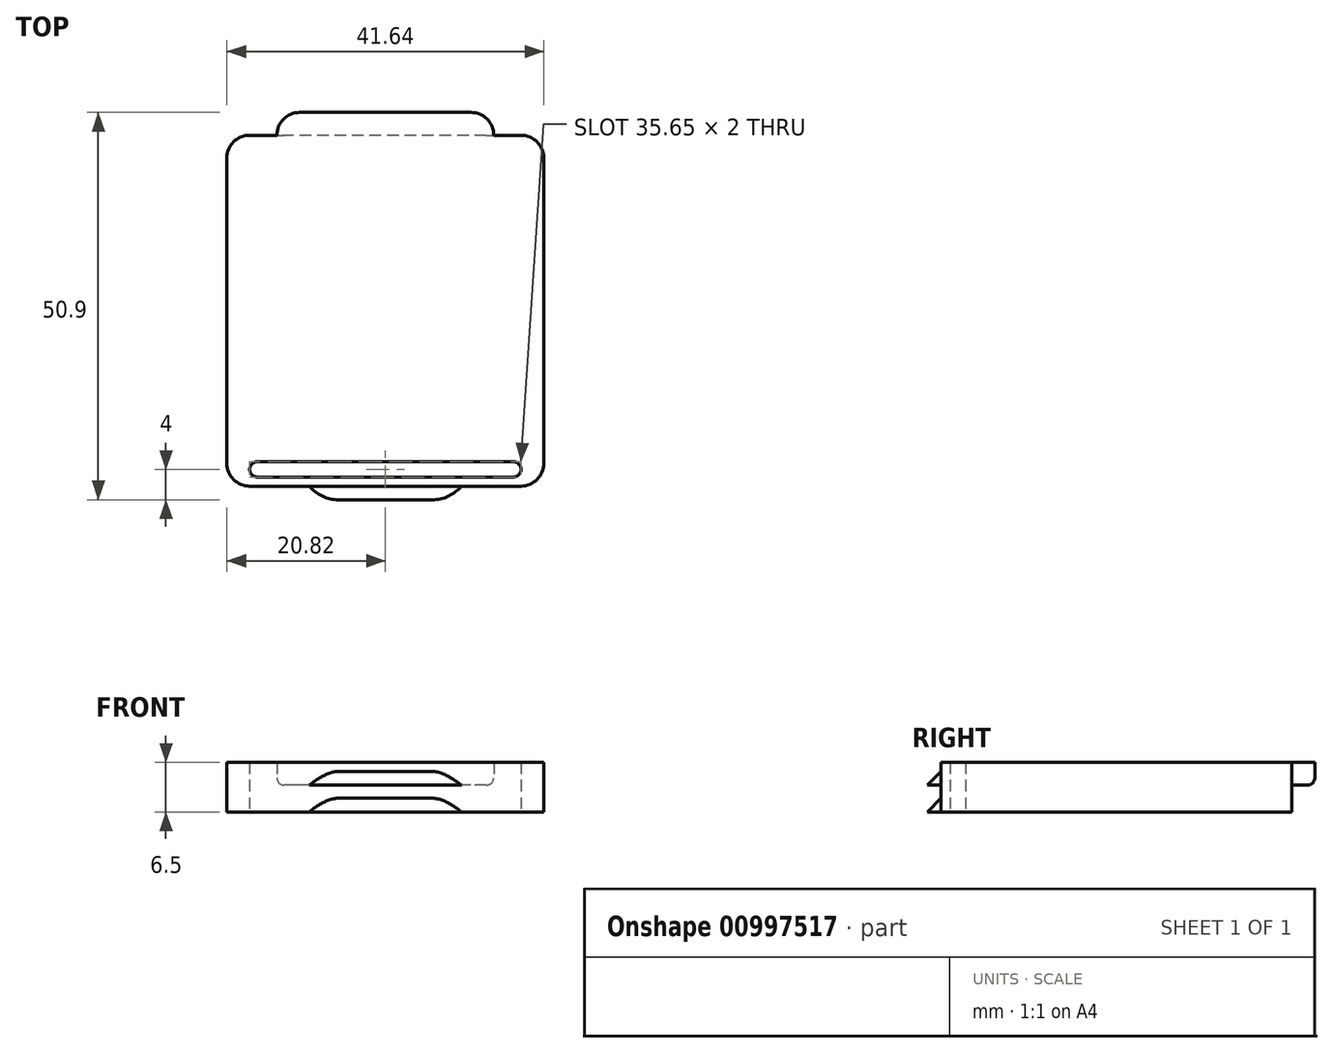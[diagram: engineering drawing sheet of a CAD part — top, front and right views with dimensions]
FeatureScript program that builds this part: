
annotation { "Feature Type Name" : "Feature", "Feature Type Description" : "" }
export const myFeature = defineFeature(function(context is Context, id is Id, definition is map)
    precondition{}
    {
        {
            var Q0;
            Q0=qCreatedBy(makeId("Top.planeOp"),FACE);
            var sketch = newSketch(context, id + "F0", { "sketchPlane" : qUnion([Q0])});
            skLineSegment(sketch, "E0.bottom", {"start": v(20.82, 23.05) * mm, "end": v(-20.83, 23.05) * mm});
            skLineSegment(sketch, "E0.top", {"start": v(20.83, -23.05) * mm, "end": v(-20.82, -23.05) * mm});
            skLineSegment(sketch, "E0.left", {"start": v(20.82, 23.05) * mm, "end": v(20.83, -23.05) * mm});
            skLineSegment(sketch, "E0.right", {"start": v(-20.83, 23.05) * mm, "end": v(-20.82, -23.05) * mm});
            skPoint(sketch, "E0.middle", {"position": v(0, 0) * mm});
            skPoint(sketch, "E1.visualSharp", {"position": v(-20.83, 23.05) * mm});
            skPoint(sketch, "E2.visualSharp", {"position": v(20.82, 23.05) * mm});
            skPoint(sketch, "E3.visualSharp", {"position": v(20.83, -23.05) * mm});
            skPoint(sketch, "E4.visualSharp", {"position": v(-20.82, -23.05) * mm});
            skLineSegment(sketch, "E5.0", {"start": v(16.83, -21.85) * mm, "end": v(-16.82, -21.85) * mm});
            skLineSegment(sketch, "E6.0", {"start": v(16.83, -19.85) * mm, "end": v(-16.82, -19.85) * mm});
            skArc(sketch, "E7", {"start": v(16.83, -21.85) * mm, "mid": v(17.83, -20.85) * mm, "end": v(16.83, -19.85) * mm});
            skArc(sketch, "E8", {"start": v(-16.82, -19.85) * mm, "mid": v(-17.82, -20.85) * mm, "end": v(-16.82, -21.85) * mm});
            skSolve(sketch);
        }
        {
            var Q0;
            Q0 = qSketchRegion(id + "F0", true);
            extrude(context, id + "F1", {"entities" : qUnion([Q0]), "depth" : 6.5 * mm, "offsetDistance" : 25 * mm});
        }
        {
            var Q0;
            Q0=makeQuery(id+"F1.opExtrude","SWEPT_FACE",FACE,{"disambiguationData":[OSD([sQuery(id+"F0.wireOp",EDGE,"E0.bottom")])]});
            var sketch = newSketch(context, id + "F2", { "sketchPlane" : qUnion([Q0])});
            skLineSegment(sketch, "E9.bottom", {"start": v(-14.25, 6.5) * mm, "end": v(14.25, 6.5) * mm});
            skLineSegment(sketch, "E9.top", {"start": v(-14.25, 3.5) * mm, "end": v(14.25, 3.5) * mm});
            skLineSegment(sketch, "E9.left", {"start": v(-14.25, 6.5) * mm, "end": v(-14.25, 3.5) * mm});
            skLineSegment(sketch, "E9.right", {"start": v(14.25, 6.5) * mm, "end": v(14.25, 3.5) * mm});
            skPoint(sketch, "E9.middle.positionSnap0", {"position": v(0, 6.5) * mm});
            skSolve(sketch);
        }
        {
            var Q0;
            Q0 = qSketchRegion(id + "F2", true);
            extrude(context, id + "F3", {"entities" : qUnion([Q0]), "operationType" : NewBodyOperationType.ADD, "depth" : 3 * mm, "offsetDistance" : 25 * mm});
        }
        {
            var Q0;
            Q0=makeQuery(id+"F3.opExtrude","SWEPT_EDGE",EDGE,{"disambiguationData":[OSD([sQuery(id+"F2.wireOp",EDGE,"E9.top"),sQuery(id+"F2.wireOp",EDGE,"E9.right")])]});
            var Q1;
            Q1=makeQuery(id+"F3.opExtrude","SWEPT_EDGE",EDGE,{"disambiguationData":[OSD([sQuery(id+"F2.wireOp",EDGE,"E9.top"),sQuery(id+"F2.wireOp",EDGE,"E9.left")])]});
            var Q2;
            Q2=makeQuery(id+"F3.opExtrude","CAP_EDGE",EDGE,{"disambiguationData":[OSD([sQuery(id+"F2.wireOp",EDGE,"E9.top")])],"isStart":false});
            fillet(context, id + "F4", {"entities" : qUnion([Q0, Q1, Q2]), "radius" : 1 * mm, "tangentPropagation" : true, "allowEdgeOverflow" : false});
        }
        {
            var Q0;
            Q0=makeQuery(id+"F3.opExtrude","CAP_EDGE",EDGE,{"disambiguationData":[OSD([sQuery(id+"F2.wireOp",EDGE,"E9.left")])],"isStart":false});
            var Q1;
            Q1=makeQuery(id+"F3.opExtrude","CAP_EDGE",EDGE,{"disambiguationData":[OSD([sQuery(id+"F2.wireOp",EDGE,"E9.right")])],"isStart":false});
            var Q2;
            {var subQ0=sQuery(id+"F2.wireOp",EDGE,"E9.top");Q2=makeQuery(id+"F4.opFillet","BLEND_EDGE",EDGE,{"blendedFrom":[makeQuery(id+"F3.opExtrude","SWEPT_EDGE",EDGE,{"disambiguationData":[OSD([subQ0,sQuery(id+"F2.wireOp",EDGE,"E9.right")])]}),makeQuery(id+"F3.opExtrude","CAP_EDGE",EDGE,{"disambiguationData":[OSD([subQ0])],"isStart":false})],"blendedInto":[]});}
            fillet(context, id + "F5", {"entities" : qUnion([Q0, Q1, Q2]), "radius" : 3 * mm, "tangentPropagation" : true, "defaultsChanged" : true, "vertexSettings" : [], "allowEdgeOverflow" : false});
        }
        {
            var Q0;
            Q0=makeQuery(id+"F1.opExtrude","SWEPT_FACE",FACE,{"disambiguationData":[OSD([sQuery(id+"F0.wireOp",EDGE,"E0.top")])]});
            var sketch = newSketch(context, id + "F6", { "sketchPlane" : qUnion([Q0])});
            skLineSegment(sketch, "E10.bottom", {"start": v(-10, 5.3) * mm, "end": v(10, 5.3) * mm});
            skLineSegment(sketch, "E10.top", {"start": v(-10, 3.5) * mm, "end": v(10, 3.5) * mm});
            skLineSegment(sketch, "E10.left", {"start": v(-10, 5.3) * mm, "end": v(-10, 3.5) * mm});
            skLineSegment(sketch, "E10.right", {"start": v(10, 5.3) * mm, "end": v(10, 3.5) * mm});
            skPoint(sketch, "E10.middle", {"position": v(0, 4.4) * mm});
            skPoint(sketch, "E10.middle.positionSnap0", {"position": v(0, 6.5) * mm});
            skPoint(sketch, "E10.centerSnap0", {"position": v(0, 6.5) * mm});
            skLineSegment(sketch, "E11.bottom", {"start": v(-10, 1.8) * mm, "end": v(10, 1.8) * mm});
            skLineSegment(sketch, "E11.top", {"start": v(-10, 0) * mm, "end": v(10, 0) * mm});
            skLineSegment(sketch, "E11.left", {"start": v(-10, 1.8) * mm, "end": v(-10, 0) * mm});
            skLineSegment(sketch, "E11.right", {"start": v(10, 1.8) * mm, "end": v(10, 0) * mm});
            skPoint(sketch, "E11.middle", {"position": v(0, 0.9) * mm});
            skSolve(sketch);
        }
        {
            var Q0;
            Q0 = qSketchRegion(id + "F6", true);
            extrude(context, id + "F7", {"entities" : qUnion([Q0]), "operationType" : NewBodyOperationType.ADD, "depth" : 1.8 * mm, "offsetDistance" : 25 * mm});
        }
        {
            var Q0;
            Q0=makeQuery(id+"F7.opExtrude","CAP_EDGE",EDGE,{"disambiguationData":[OSD([sQuery(id+"F6.wireOp",EDGE,"E10.left")])],"isStart":false});
            var Q1;
            Q1=makeQuery(id+"F7.opExtrude","CAP_EDGE",EDGE,{"disambiguationData":[OSD([sQuery(id+"F6.wireOp",EDGE,"E10.right")])],"isStart":false});
            var Q2;
            Q2=makeQuery(id+"F7.opExtrude","CAP_EDGE",EDGE,{"disambiguationData":[OSD([sQuery(id+"F6.wireOp",EDGE,"E11.left")])],"isStart":false});
            var Q3;
            Q3=makeQuery(id+"F7.opExtrude","CAP_EDGE",EDGE,{"disambiguationData":[OSD([sQuery(id+"F6.wireOp",EDGE,"E11.right")])],"isStart":false});
            fillet(context, id + "F8", {"entities" : qUnion([Q0, Q1, Q2, Q3]), "tangentPropagation" : true, "radius" : 5 * mm, "defaultsChanged" : true, "vertexSettings" : [], "allowEdgeOverflow" : false});
        }
        {
            var Q0;
            Q0=makeQuery(id+"F7.opExtrude","CAP_EDGE",EDGE,{"disambiguationData":[OSD([sQuery(id+"F6.wireOp",EDGE,"E10.bottom")])],"isStart":false});
            var Q1;
            Q1=makeQuery(id+"F7.opExtrude","CAP_EDGE",EDGE,{"disambiguationData":[OSD([sQuery(id+"F6.wireOp",EDGE,"E11.bottom")])],"isStart":false});
            chamfer(context, id + "F9", {"entities" : qUnion([Q0, Q1]), "chamferType" : ChamferType.TWO_OFFSETS, "width1" : 1.8 * mm, "oppositeDirection" : false, "width2" : 1.8 * mm, "tangentPropagation" : true});
        }
        {
            var Q0;
            Q0=makeQuery(id+"F1.opExtrude","SWEPT_EDGE",EDGE,{"disambiguationData":[OSD([sQuery(id+"F0.wireOp",EDGE,"E0.top"),sQuery(id+"F0.wireOp",EDGE,"E0.left")])]});
            var Q1;
            Q1=makeQuery(id+"F1.opExtrude","SWEPT_EDGE",EDGE,{"disambiguationData":[OSD([sQuery(id+"F0.wireOp",EDGE,"E0.bottom"),sQuery(id+"F0.wireOp",EDGE,"E0.left")])]});
            var Q2;
            Q2=makeQuery(id+"F1.opExtrude","SWEPT_EDGE",EDGE,{"disambiguationData":[OSD([sQuery(id+"F0.wireOp",EDGE,"E0.bottom"),sQuery(id+"F0.wireOp",EDGE,"E0.right")])]});
            var Q3;
            Q3=makeQuery(id+"F1.opExtrude","SWEPT_EDGE",EDGE,{"disambiguationData":[OSD([sQuery(id+"F0.wireOp",EDGE,"E0.top"),sQuery(id+"F0.wireOp",EDGE,"E0.right")])]});
            fillet(context, id + "F10", {"entities" : qUnion([Q0, Q1, Q2, Q3]), "tangentPropagation" : true, "radius" : 3 * mm, "defaultsChanged" : true, "vertexSettings" : [], "allowEdgeOverflow" : false});
        }
    });
